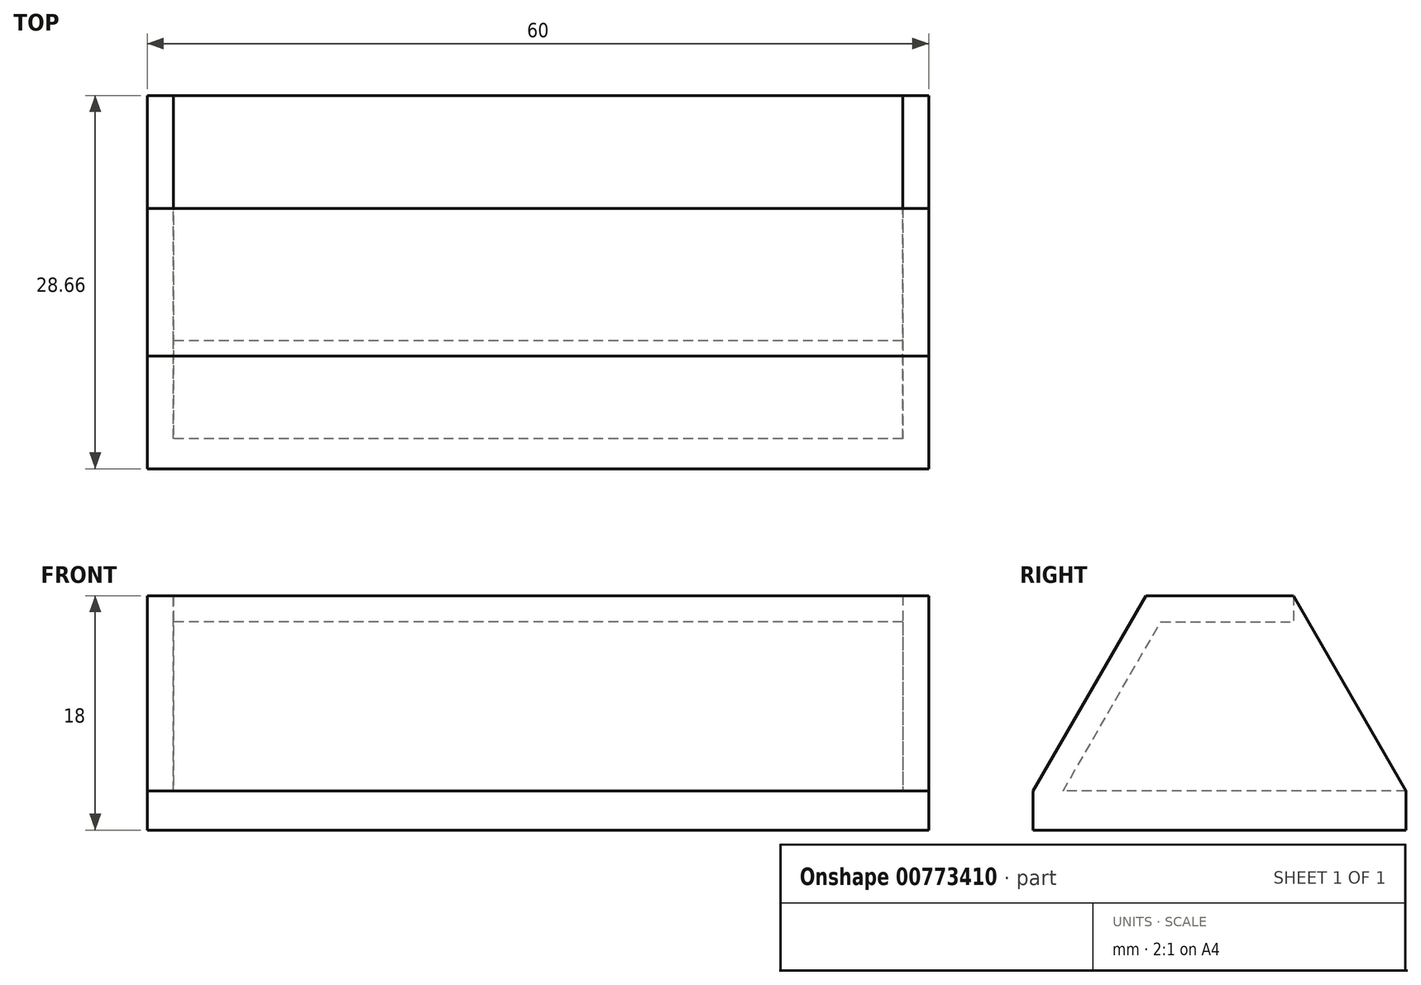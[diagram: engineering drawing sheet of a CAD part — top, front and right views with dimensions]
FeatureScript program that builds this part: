
annotation { "Feature Type Name" : "Feature", "Feature Type Description" : "" }
export const myFeature = defineFeature(function(context is Context, id is Id, definition is map)
    precondition{}
    {
        {
            var Q0;
            Q0=qCreatedBy(makeId("Top.planeOp"),FACE);
            var sketch = newSketch(context, id + "F0", { "sketchPlane" : qUnion([Q0])});
            skLineSegment(sketch, "E0.bottom", {"start": v(-30, -15) * mm, "end": v(30, -15) * mm});
            skLineSegment(sketch, "E0.top", {"start": v(-30, 15) * mm, "end": v(30, 15) * mm});
            skLineSegment(sketch, "E0.left", {"start": v(-30, -15) * mm, "end": v(-30, 15) * mm});
            skLineSegment(sketch, "E0.right", {"start": v(30, -15) * mm, "end": v(30, 15) * mm});
            skPoint(sketch, "E0.middle", {"position": v(0, 0) * mm});
            skSolve(sketch);
        }
        {
            var Q0;
            Q0=makeQuery(id+"F0.imprint","IMPRINT",FACE,{"disambiguationData":[TD([[makeQuery(id+"F0.imprint","IMPRINT",EDGE,{"derivedFrom":sQuery(id+"F0.wireOp",EDGE,"E0.bottom")}),1.0]])]});
            extrude(context, id + "F1", {"entities" : qUnion([Q0]), "depth" : 3 * mm, "offsetDistance" : 25 * mm});
        }
        {
            var Q0;
            Q0=makeQuery(id+"F1.opExtrude","SWEPT_FACE",FACE,{"disambiguationData":[OSD([sQuery(id+"F0.wireOp",EDGE,"E0.right")])]});
            var sketch = newSketch(context, id + "F2", { "sketchPlane" : qUnion([Q0])});
            skLineSegment(sketch, "E1.bottom", {"start": v(-15, 3) * mm, "end": v(0, 3) * mm});
            skLineSegment(sketch, "E1.top", {"start": v(-15, 18) * mm, "end": v(0, 18) * mm});
            skLineSegment(sketch, "E1.left", {"start": v(-15, 3) * mm, "end": v(-15, 18) * mm});
            skLineSegment(sketch, "E1.right", {"start": v(0, 3) * mm, "end": v(0, 18) * mm});
            skSolve(sketch);
        }
        {
            var Q0;
            Q0=makeQuery(id+"F2.imprint","IMPRINT",FACE,{"disambiguationData":[TD([[makeQuery(id+"F2.imprint","IMPRINT",EDGE,{"derivedFrom":sQuery(id+"F2.wireOp",EDGE,"E1.bottom")}),1.0]])]});
            extrude(context, id + "F3", {"entities" : qUnion([Q0]), "operationType" : NewBodyOperationType.ADD, "oppositeDirection" : true, "depth" : 60 * mm, "offsetDistance" : 25 * mm});
        }
        {
            var Q0;
            Q0=makeQuery(id+"F3.boolean.opBoolean","MERGE",FACE,{"derivedFrom":[makeQuery(id+"F1.opExtrude","SWEPT_FACE",FACE,{"disambiguationData":[OSD([sQuery(id+"F0.wireOp",EDGE,"E0.right")])]}),makeQuery(id+"F3.opExtrude","CAP_FACE",FACE,{"disambiguationData":[OSD([sQuery(id+"F2.wireOp",EDGE,"E1.bottom"),sQuery(id+"F2.wireOp",EDGE,"E1.top"),sQuery(id+"F2.wireOp",EDGE,"E1.left"),sQuery(id+"F2.wireOp",EDGE,"E1.right")])],"isStart":true})]});
            var sketch = newSketch(context, id + "F4", { "sketchPlane" : qUnion([Q0])});
            skLineSegment(sketch, "E2.bottom", {"start": v(0, 3) * mm, "end": v(5, 3) * mm});
            skLineSegment(sketch, "E2.top", {"start": v(0, 18) * mm, "end": v(5, 18) * mm});
            skLineSegment(sketch, "E2.left", {"start": v(0, 3) * mm, "end": v(0, 18) * mm});
            skLineSegment(sketch, "E2.right", {"start": v(5, 3) * mm, "end": v(5, 18) * mm});
            skSolve(sketch);
        }
        {
            var Q0;
            Q0=makeQuery(id+"F4.imprint","IMPRINT",FACE,{"disambiguationData":[TD([[makeQuery(id+"F4.imprint","IMPRINT",EDGE,{"derivedFrom":sQuery(id+"F4.wireOp",EDGE,"E2.bottom")}),1.0]])]});
            extrude(context, id + "F5", {"entities" : qUnion([Q0]), "operationType" : NewBodyOperationType.ADD, "oppositeDirection" : true, "depth" : 60 * mm, "offsetDistance" : 25 * mm});
        }
        {
            var Q0;
            Q0=makeQuery(id+"F5.boolean.opBoolean","MERGE",FACE,{"derivedFrom":[makeQuery(id+"F3.boolean.opBoolean","MERGE",FACE,{"derivedFrom":[makeQuery(id+"F1.opExtrude","SWEPT_FACE",FACE,{"disambiguationData":[OSD([sQuery(id+"F0.wireOp",EDGE,"E0.right")])]}),makeQuery(id+"F3.opExtrude","CAP_FACE",FACE,{"disambiguationData":[OSD([sQuery(id+"F2.wireOp",EDGE,"E1.bottom"),sQuery(id+"F2.wireOp",EDGE,"E1.top"),sQuery(id+"F2.wireOp",EDGE,"E1.left"),sQuery(id+"F2.wireOp",EDGE,"E1.right")])],"isStart":true})]}),makeQuery(id+"F5.opExtrude","CAP_FACE",FACE,{"disambiguationData":[OSD([sQuery(id+"F4.wireOp",EDGE,"E2.bottom"),sQuery(id+"F4.wireOp",EDGE,"E2.top"),sQuery(id+"F4.wireOp",EDGE,"E2.left"),sQuery(id+"F4.wireOp",EDGE,"E2.right")])],"isStart":true})]});
            var sketch = newSketch(context, id + "F6", { "sketchPlane" : qUnion([Q0])});
            skLineSegment(sketch, "E3", {"start": v(-15, 3) * mm, "end": v(-6.34, 18) * mm});
            skLineSegment(sketch, "E4", {"start": v(-6.34, 18) * mm, "end": v(-15, 18) * mm});
            skSolve(sketch);
        }
        {
            var Q0;
            {var subQ0=sQuery(id+"F6.wireOp",EDGE,"E3");Q0=makeQuery(id+"F6.imprint","IMPRINT",FACE,{"disambiguationData":[TD([[makeQuery(id+"F6.imprint","IMPRINT",EDGE,{"derivedFrom":subQ0}),1.0]])]});}
            extrude(context, id + "F7", {"entities" : qUnion([Q0]), "operationType" : NewBodyOperationType.REMOVE, "endBound" : BoundingType.UP_TO_NEXT, "oppositeDirection" : true, "depth" : 25 * mm, "offsetDistance" : 25 * mm});
        }
        {
            var Q0;
            Q0=makeQuery(id+"F5.boolean.opBoolean","MERGE",FACE,{"derivedFrom":[makeQuery(id+"F3.boolean.opBoolean","MERGE",FACE,{"derivedFrom":[makeQuery(id+"F1.opExtrude","SWEPT_FACE",FACE,{"disambiguationData":[OSD([sQuery(id+"F0.wireOp",EDGE,"E0.left")])]}),makeQuery(id+"F3.opExtrude","CAP_FACE",FACE,{"disambiguationData":[OSD([sQuery(id+"F2.wireOp",EDGE,"E1.bottom"),sQuery(id+"F2.wireOp",EDGE,"E1.top"),sQuery(id+"F2.wireOp",EDGE,"E1.left"),sQuery(id+"F2.wireOp",EDGE,"E1.right")])],"isStart":false})]}),makeQuery(id+"F5.opExtrude","CAP_FACE",FACE,{"disambiguationData":[OSD([sQuery(id+"F4.wireOp",EDGE,"E2.bottom"),sQuery(id+"F4.wireOp",EDGE,"E2.top"),sQuery(id+"F4.wireOp",EDGE,"E2.left"),sQuery(id+"F4.wireOp",EDGE,"E2.right")])],"isStart":false})]});
            var sketch = newSketch(context, id + "F8", { "sketchPlane" : qUnion([Q0])});
            skLineSegment(sketch, "E5", {"start": v(-5, 3) * mm, "end": v(-5, 16) * mm});
            skLineSegment(sketch, "E6", {"start": v(-5, 16) * mm, "end": v(5.19, 16) * mm});
            skLineSegment(sketch, "E7", {"start": v(5.19, 16) * mm, "end": v(12.7, 3) * mm});
            skLineSegment(sketch, "E8", {"start": v(12.7, 3) * mm, "end": v(-5, 3) * mm});
            skSolve(sketch);
        }
        {
            var Q0;
            Q0=makeQuery(id+"F8.imprint","IMPRINT",FACE,{"disambiguationData":[TD([[makeQuery(id+"F8.imprint","IMPRINT",EDGE,{"derivedFrom":sQuery(id+"F8.wireOp",EDGE,"E5")}),-1.0]])]});
            extrude(context, id + "F9", {"entities" : qUnion([Q0]), "operationType" : NewBodyOperationType.REMOVE, "oppositeDirection" : true, "depth" : 58 * mm, "offsetDistance" : 25 * mm});
        }
        {
            var Q0;
            Q0=makeQuery(id+"F5.boolean.opBoolean","MERGE",FACE,{"derivedFrom":[makeQuery(id+"F3.boolean.opBoolean","MERGE",FACE,{"derivedFrom":[makeQuery(id+"F1.opExtrude","SWEPT_FACE",FACE,{"disambiguationData":[OSD([sQuery(id+"F0.wireOp",EDGE,"E0.left")])]}),makeQuery(id+"F3.opExtrude","CAP_FACE",FACE,{"disambiguationData":[OSD([sQuery(id+"F2.wireOp",EDGE,"E1.bottom"),sQuery(id+"F2.wireOp",EDGE,"E1.top"),sQuery(id+"F2.wireOp",EDGE,"E1.left"),sQuery(id+"F2.wireOp",EDGE,"E1.right")])],"isStart":false})]}),makeQuery(id+"F5.opExtrude","CAP_FACE",FACE,{"disambiguationData":[OSD([sQuery(id+"F4.wireOp",EDGE,"E2.bottom"),sQuery(id+"F4.wireOp",EDGE,"E2.top"),sQuery(id+"F4.wireOp",EDGE,"E2.left"),sQuery(id+"F4.wireOp",EDGE,"E2.right")])],"isStart":false})]});
            var sketch = newSketch(context, id + "F10", { "sketchPlane" : qUnion([Q0])});
            skLineSegment(sketch, "E9", {"start": v(-5, 18) * mm, "end": v(-5, 0) * mm});
            skLineSegment(sketch, "E10", {"start": v(-5, 0) * mm, "end": v(15, 0) * mm});
            skLineSegment(sketch, "E11", {"start": v(15, 0) * mm, "end": v(15, 3) * mm});
            skLineSegment(sketch, "E12", {"start": v(15, 3) * mm, "end": v(6.34, 18) * mm});
            skLineSegment(sketch, "E13", {"start": v(6.34, 18) * mm, "end": v(-5, 18) * mm});
            skSolve(sketch);
        }
        {
            var Q0;
            {var subQ0=sQuery(id+"F10.wireOp",EDGE,"E10");Q0=makeQuery(id+"F10.imprint","IMPRINT",FACE,{"disambiguationData":[TD([[makeQuery(id+"F10.imprint","IMPRINT",EDGE,{"derivedFrom":subQ0}),-1.0]])]});}
            var Q1;
            {var subQ1=makeQuery(id+"F9.boolean.opBoolean","COPY",EDGE,{"derivedFrom":makeQuery(id+"F9.opExtrude","CAP_EDGE",EDGE,{"disambiguationData":[OSD([sQuery(id+"F8.wireOp",EDGE,"E6")])],"isStart":true})});Q1=makeQuery(id+"F10.imprint","IMPRINT",FACE,{"disambiguationData":[TD([[makeQuery(id+"F10.imprint","IMPRINT",EDGE,{"derivedFrom":subQ1}),-1.0]])]});}
            extrude(context, id + "F11", {"entities" : qUnion([Q0, Q1]), "operationType" : NewBodyOperationType.ADD, "oppositeDirection" : true, "depth" : 2 * mm, "offsetDistance" : 25 * mm});
        }
        {
            var Q0;
            Q0=makeQuery(id+"F11.boolean.opBoolean","MERGE",FACE,{"derivedFrom":[makeQuery(id+"F5.boolean.opBoolean","MERGE",FACE,{"derivedFrom":[makeQuery(id+"F3.boolean.opBoolean","MERGE",FACE,{"derivedFrom":[makeQuery(id+"F1.opExtrude","SWEPT_FACE",FACE,{"disambiguationData":[OSD([sQuery(id+"F0.wireOp",EDGE,"E0.left")])]}),makeQuery(id+"F3.opExtrude","CAP_FACE",FACE,{"disambiguationData":[OSD([sQuery(id+"F2.wireOp",EDGE,"E1.bottom"),sQuery(id+"F2.wireOp",EDGE,"E1.top"),sQuery(id+"F2.wireOp",EDGE,"E1.left"),sQuery(id+"F2.wireOp",EDGE,"E1.right")])],"isStart":false})]}),makeQuery(id+"F5.opExtrude","CAP_FACE",FACE,{"disambiguationData":[OSD([sQuery(id+"F4.wireOp",EDGE,"E2.bottom"),sQuery(id+"F4.wireOp",EDGE,"E2.top"),sQuery(id+"F4.wireOp",EDGE,"E2.left"),sQuery(id+"F4.wireOp",EDGE,"E2.right")])],"isStart":false})]}),makeQuery(id+"F11.opExtrude","CAP_FACE",FACE,{"disambiguationData":[OSD([sQuery(id+"F10.wireOp",EDGE,"E9"),sQuery(id+"F10.wireOp",EDGE,"E10"),sQuery(id+"F10.wireOp",EDGE,"E11"),sQuery(id+"F10.wireOp",EDGE,"E12"),sQuery(id+"F10.wireOp",EDGE,"E13")])],"isStart":true})]});
            var sketch = newSketch(context, id + "F12", { "sketchPlane" : qUnion([Q0])});
            skLineSegment(sketch, "E14", {"start": v(-5, 18) * mm, "end": v(-13.66, 3) * mm});
            skSolve(sketch);
        }
        {
            var Q0;
            {var subQ0=sQuery(id+"F12.wireOp",EDGE,"E14");Q0=makeQuery(id+"F12.imprint","IMPRINT",FACE,{"disambiguationData":[TD([[makeQuery(id+"F12.imprint","IMPRINT",EDGE,{"derivedFrom":subQ0}),1.0]])]});}
            var Q1;
            {var subQ3=sQuery(id+"F0.wireOp",EDGE,"E0.left");Q1=makeQuery(id+"F12.imprint","IMPRINT",FACE,{"disambiguationData":[TD([[makeQuery(id+"F12.imprint","IMPRINT",EDGE,{"derivedFrom":makeQuery(id+"F1.opExtrude","CAP_EDGE",EDGE,{"disambiguationData":[OSD([subQ3])],"isStart":true})}),-1.0]])]});}
            extrude(context, id + "F13", {"entities" : qUnion([Q0, Q1]), "operationType" : NewBodyOperationType.ADD, "oppositeDirection" : true, "depth" : 2 * mm, "offsetDistance" : 25 * mm});
        }
        {
            var Q0;
            Q0=makeQuery(id+"F5.boolean.opBoolean","MERGE",FACE,{"derivedFrom":[makeQuery(id+"F3.boolean.opBoolean","MERGE",FACE,{"derivedFrom":[makeQuery(id+"F1.opExtrude","SWEPT_FACE",FACE,{"disambiguationData":[OSD([sQuery(id+"F0.wireOp",EDGE,"E0.right")])]}),makeQuery(id+"F3.opExtrude","CAP_FACE",FACE,{"disambiguationData":[OSD([sQuery(id+"F2.wireOp",EDGE,"E1.bottom"),sQuery(id+"F2.wireOp",EDGE,"E1.top"),sQuery(id+"F2.wireOp",EDGE,"E1.left"),sQuery(id+"F2.wireOp",EDGE,"E1.right")])],"isStart":true})]}),makeQuery(id+"F5.opExtrude","CAP_FACE",FACE,{"disambiguationData":[OSD([sQuery(id+"F4.wireOp",EDGE,"E2.bottom"),sQuery(id+"F4.wireOp",EDGE,"E2.top"),sQuery(id+"F4.wireOp",EDGE,"E2.left"),sQuery(id+"F4.wireOp",EDGE,"E2.right")])],"isStart":true})]});
            var sketch = newSketch(context, id + "F14", { "sketchPlane" : qUnion([Q0])});
            skLineSegment(sketch, "E15", {"start": v(5, 18) * mm, "end": v(13.66, 3) * mm});
            skSolve(sketch);
        }
        {
            var Q0;
            {var subQ1=sQuery(id+"F0.wireOp",EDGE,"E0.right");Q0=makeQuery(id+"F14.imprint","IMPRINT",FACE,{"disambiguationData":[TD([[makeQuery(id+"F14.imprint","IMPRINT",EDGE,{"derivedFrom":makeQuery(id+"F1.opExtrude","CAP_EDGE",EDGE,{"disambiguationData":[OSD([subQ1])],"isStart":true})}),1.0]])]});}
            var Q1;
            {var subQ0=sQuery(id+"F14.wireOp",EDGE,"E15");Q1=makeQuery(id+"F14.imprint","IMPRINT",FACE,{"disambiguationData":[TD([[makeQuery(id+"F14.imprint","IMPRINT",EDGE,{"derivedFrom":subQ0}),-1.0]])]});}
            extrude(context, id + "F15", {"entities" : qUnion([Q0, Q1]), "operationType" : NewBodyOperationType.ADD, "oppositeDirection" : true, "depth" : 2 * mm, "offsetDistance" : 25 * mm});
        }
        {
            var Q0;
            {var subQ0=sQuery(id+"F4.wireOp",EDGE,"E2.top");var subQ1=sQuery(id+"F2.wireOp",EDGE,"E1.left");var subQ2=sQuery(id+"F2.wireOp",EDGE,"E1.top");var subQ3=sQuery(id+"F0.wireOp",EDGE,"E0.right");Q0=makeQuery(id+"F15.boolean.opBoolean","MERGE",FACE,{"derivedFrom":[makeQuery(id+"F5.boolean.opBoolean","MERGE",FACE,{"derivedFrom":[makeQuery(id+"F3.boolean.opBoolean","MERGE",FACE,{"derivedFrom":[makeQuery(id+"F1.opExtrude","SWEPT_FACE",FACE,{"disambiguationData":[OSD([subQ3])]}),makeQuery(id+"F3.opExtrude","CAP_FACE",FACE,{"disambiguationData":[OSD([sQuery(id+"F2.wireOp",EDGE,"E1.bottom"),subQ2,subQ1,sQuery(id+"F2.wireOp",EDGE,"E1.right")])],"isStart":true})]}),makeQuery(id+"F5.opExtrude","CAP_FACE",FACE,{"disambiguationData":[OSD([sQuery(id+"F4.wireOp",EDGE,"E2.bottom"),subQ0,sQuery(id+"F4.wireOp",EDGE,"E2.left"),sQuery(id+"F4.wireOp",EDGE,"E2.right")])],"isStart":true})]}),makeQuery(id+"F15.opExtrude","CAP_FACE",FACE,{"disambiguationData":[OSD([sQuery(id+"F0.wireOp",EDGE,"E0.bottom"),sQuery(id+"F0.wireOp",EDGE,"E0.top"),subQ3,subQ2,subQ1,subQ0,sQuery(id+"F6.wireOp",EDGE,"E3"),sQuery(id+"F14.wireOp",EDGE,"E15")])],"isStart":true})]});}
            var sketch = newSketch(context, id + "F16", { "sketchPlane" : qUnion([Q0])});
            skLineSegment(sketch, "E16", {"start": v(13.66, 3) * mm, "end": v(13.66, 0) * mm});
            skSolve(sketch);
        }
        {
            var Q0;
            {var subQ0=sQuery(id+"F16.wireOp",EDGE,"E16");Q0=makeQuery(id+"F16.imprint","IMPRINT",FACE,{"disambiguationData":[TD([[makeQuery(id+"F16.imprint","IMPRINT",EDGE,{"derivedFrom":subQ0}),1.0]])]});}
            extrude(context, id + "F17", {"entities" : qUnion([Q0]), "operationType" : NewBodyOperationType.REMOVE, "oppositeDirection" : true, "depth" : 60 * mm, "offsetDistance" : 25 * mm});
        }
    });
